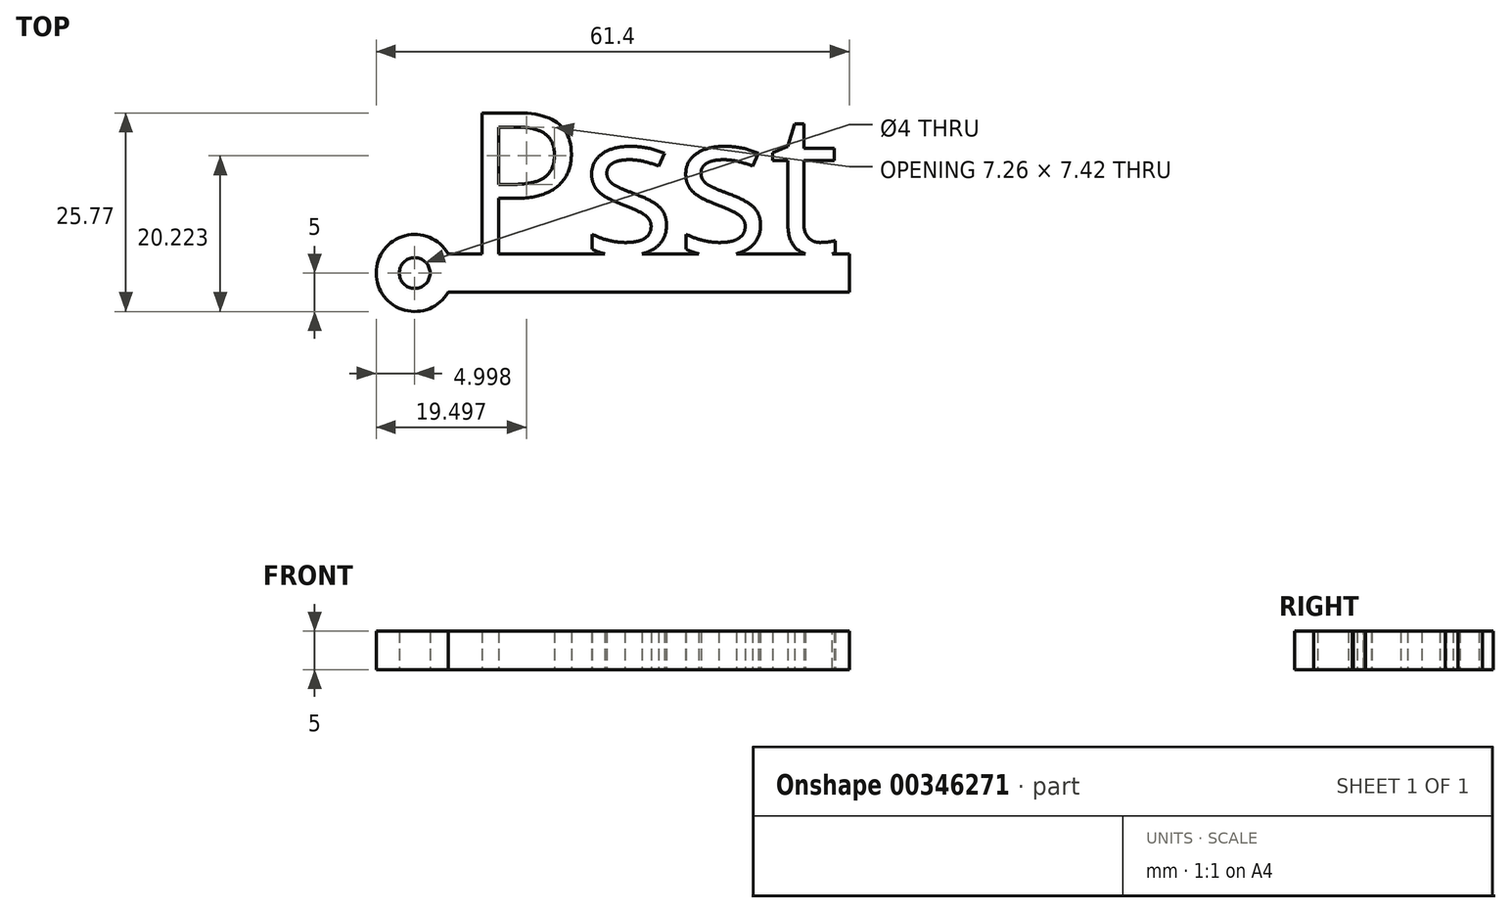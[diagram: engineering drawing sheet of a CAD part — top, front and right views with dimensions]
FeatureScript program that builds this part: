
annotation { "Feature Type Name" : "Feature", "Feature Type Description" : "" }
export const myFeature = defineFeature(function(context is Context, id is Id, definition is map)
    precondition{}
    {
        {
            var Q0;
            Q0=qCreatedBy(makeId("Top.planeOp"),FACE);
            var sketch = newSketch(context, id + "F0", { "sketchPlane" : qUnion([Q0])});
            skText(sketch, "E0", { "text": "Psst\n", "fontName": "OpenSans-Regular.ttf"});
            skLineSegment(sketch, "E1.bottom", {"start": v(-22.57, 0) * mm, "end": v(29.5, 0) * mm});
            skLineSegment(sketch, "E1.top", {"start": v(-22.57, -5) * mm, "end": v(29.5, -5) * mm});
            skLineSegment(sketch, "E1.right", {"start": v(29.5, 0) * mm, "end": v(29.5, -5) * mm});
            skCircle(sketch, "E2", {"center": v(-26.9, -2.5) * mm, "radius": 5 * mm});
            skPoint(sketch, "E2.centerSnap0", {"position": v(-22.79, -2.5) * mm});
            skCircle(sketch, "E3", {"center": v(-26.9, -2.5) * mm, "radius": 2 * mm});
            skPoint(sketch, "E4.orphan", {"position": v(-22.79, 0) * mm});
            skPoint(sketch, "E5.orphan", {"position": v(-22.79, -5) * mm});
            const initialGuessF0  = {"E0": [-0.02067, 0, 1, 0, 0.01843]};
            skSetInitialGuess(sketch, initialGuessF0);
            skSolve(sketch);
        }
        {
            var Q0;
            Q0 = qSketchRegion(id + "F0", true);
            extrude(context, id + "F1", {"entities" : qUnion([Q0]), "depth" : 5 * mm});
        }
    });
